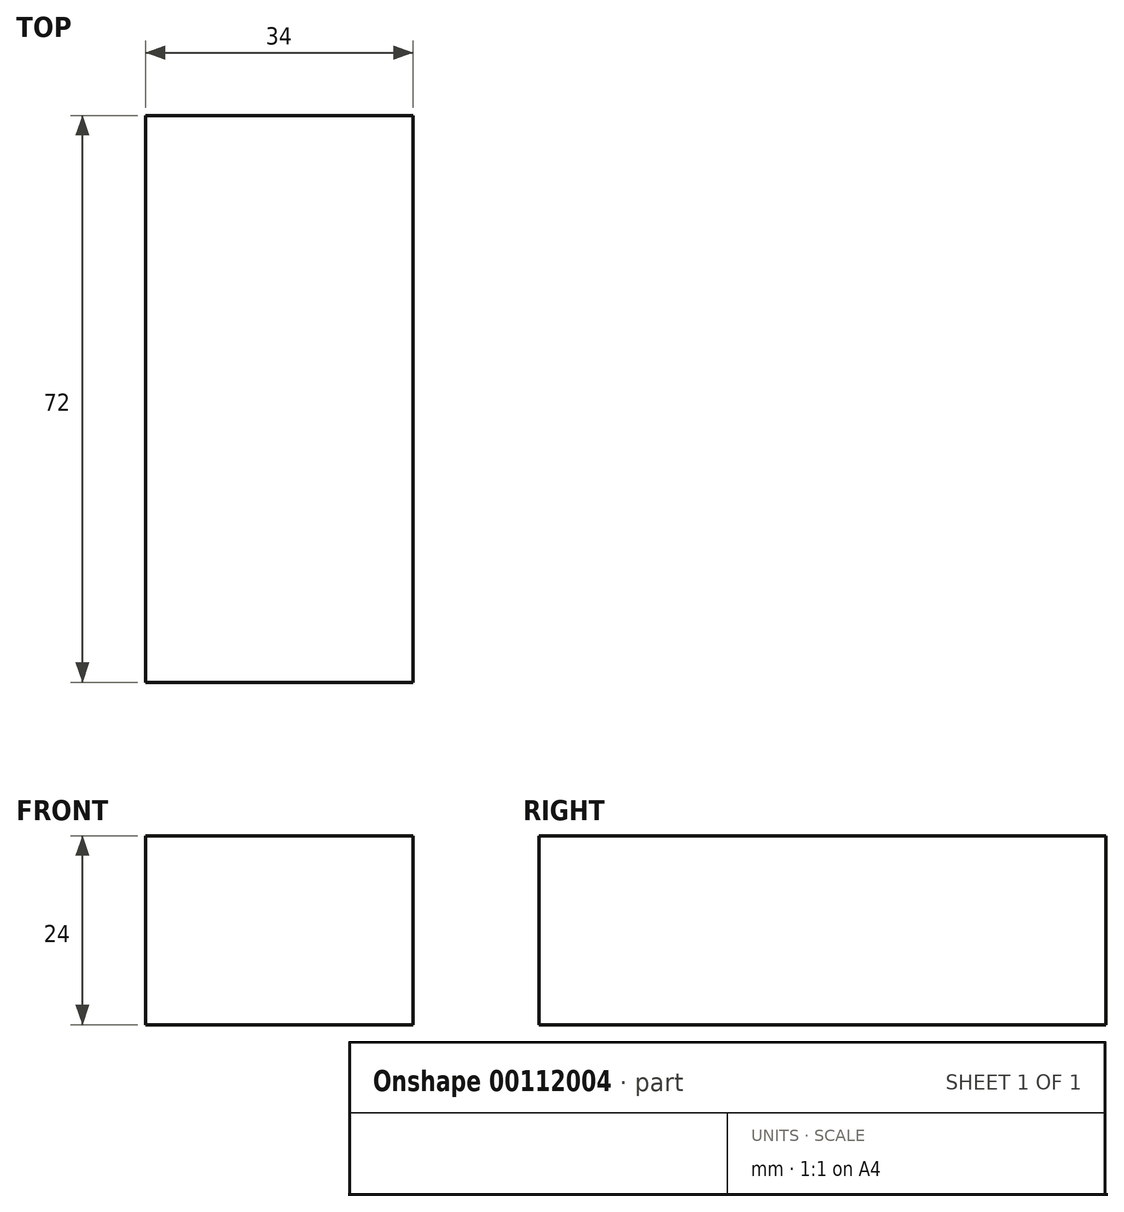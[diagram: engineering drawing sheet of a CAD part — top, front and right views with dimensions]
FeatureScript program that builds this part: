
annotation { "Feature Type Name" : "Feature", "Feature Type Description" : "" }
export const myFeature = defineFeature(function(context is Context, id is Id, definition is map)
    precondition{}
    {
        {
            var Q0;
            Q0=qCreatedBy(makeId("Top.planeOp"),FACE);
            var sketch = newSketch(context, id + "F0", { "sketchPlane" : qUnion([Q0])});
            skLineSegment(sketch, "E0.bottom", {"start": v(0, 0) * mm, "end": v(34, 0) * mm});
            skLineSegment(sketch, "E0.top", {"start": v(0, -72) * mm, "end": v(34, -72) * mm});
            skLineSegment(sketch, "E0.left", {"start": v(0, 0) * mm, "end": v(0, -72) * mm});
            skLineSegment(sketch, "E0.right", {"start": v(34, 0) * mm, "end": v(34, -72) * mm});
            skSolve(sketch);
        }
        {
            var Q0;
            Q0 = qSketchRegion(id + "F0", true);
            extrude(context, id + "F1", {"entities" : qUnion([Q0]), "depth" : 24 * mm});
        }
    });
